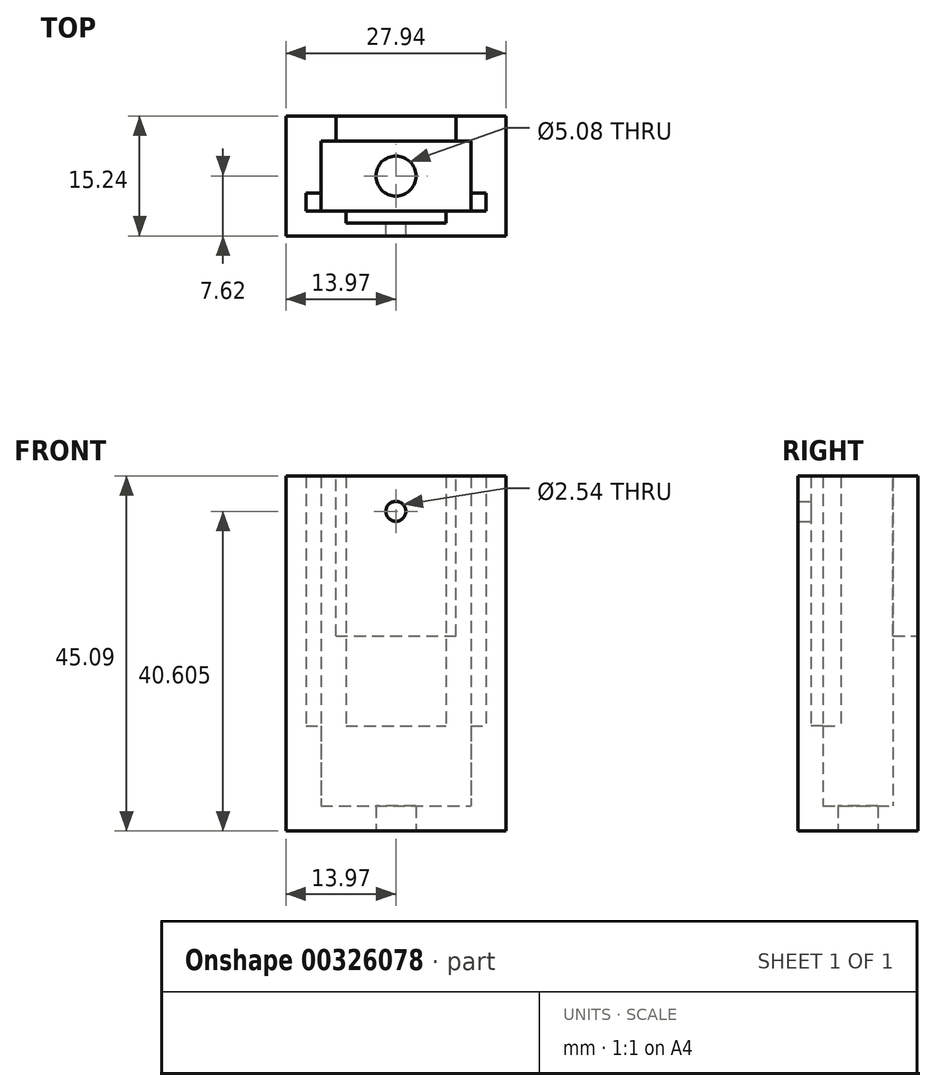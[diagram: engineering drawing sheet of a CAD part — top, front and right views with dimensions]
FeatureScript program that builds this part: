
annotation { "Feature Type Name" : "Feature", "Feature Type Description" : "" }
export const myFeature = defineFeature(function(context is Context, id is Id, definition is map)
    precondition{}
    {
        {
            var Q0;
            Q0=qCreatedBy(makeId("Top.planeOp"),FACE);
            var sketch = newSketch(context, id + "F0", { "sketchPlane" : qUnion([Q0])});
            skLineSegment(sketch, "E0.bottom", {"start": v(-13.97, -7.62) * mm, "end": v(13.97, -7.62) * mm});
            skLineSegment(sketch, "E0.top", {"start": v(-13.97, 7.62) * mm, "end": v(13.97, 7.62) * mm});
            skLineSegment(sketch, "E0.left", {"start": v(-13.97, -7.62) * mm, "end": v(-13.97, 7.62) * mm});
            skLineSegment(sketch, "E0.right", {"start": v(13.97, -7.62) * mm, "end": v(13.97, 7.62) * mm});
            skPoint(sketch, "E0.middle", {"position": v(0, 0) * mm});
            skCircle(sketch, "E1", {"center": v(0, 0) * mm, "radius": 2.54 * mm});
            skSolve(sketch);
        }
        {
            var Q0;
            Q0=makeQuery(id+"F0.imprint","IMPRINT",FACE,{"disambiguationData":[TD([[makeQuery(id+"F0.imprint","IMPRINT",EDGE,{"derivedFrom":sQuery(id+"F0.wireOp",EDGE,"E0.bottom")}),1.0]])]});
            extrude(context, id + "F1", {"entities" : qUnion([Q0]), "depth" : 3.17 * mm});
        }
        {
            var Q0;
            Q0=makeQuery(id+"F1.opExtrude","CAP_FACE",FACE,{"disambiguationData":[OSD([sQuery(id+"F0.wireOp",EDGE,"E0.bottom"),sQuery(id+"F0.wireOp",EDGE,"E0.top"),sQuery(id+"F0.wireOp",EDGE,"E0.left"),sQuery(id+"F0.wireOp",EDGE,"E0.right"),sQuery(id+"F0.wireOp",EDGE,"E1")])],"isStart":false});
            var sketch = newSketch(context, id + "F2", { "sketchPlane" : qUnion([Q0])});
            skLineSegment(sketch, "E2.bottom", {"start": v(-9.53, -4.45) * mm, "end": v(9.53, -4.45) * mm});
            skLineSegment(sketch, "E2.top", {"start": v(-9.53, 4.45) * mm, "end": v(9.53, 4.45) * mm});
            skLineSegment(sketch, "E2.left", {"start": v(-9.53, -4.45) * mm, "end": v(-9.53, 4.45) * mm});
            skLineSegment(sketch, "E2.right", {"start": v(9.53, -4.45) * mm, "end": v(9.53, 4.45) * mm});
            skPoint(sketch, "E2.middle", {"position": v(0, 0) * mm});
            skSolve(sketch);
        }
        {
            var Q0;
            Q0=makeQuery(id+"F2.imprint","IMPRINT",FACE,{"disambiguationData":[TD([[makeQuery(id+"F2.imprint","IMPRINT",EDGE,{"derivedFrom":sQuery(id+"F2.wireOp",EDGE,"E2.bottom")}),-1.0]])]});
            extrude(context, id + "F3", {"entities" : qUnion([Q0]), "operationType" : NewBodyOperationType.ADD, "depth" : 10.16 * mm});
        }
        {
            var Q0;
            Q0=makeQuery(id+"F3.opExtrude","CAP_FACE",FACE,{"disambiguationData":[OSD([sQuery(id+"F0.wireOp",EDGE,"E0.bottom"),sQuery(id+"F0.wireOp",EDGE,"E0.top"),sQuery(id+"F0.wireOp",EDGE,"E0.left"),sQuery(id+"F0.wireOp",EDGE,"E0.right"),sQuery(id+"F2.wireOp",EDGE,"E2.bottom"),sQuery(id+"F2.wireOp",EDGE,"E2.top"),sQuery(id+"F2.wireOp",EDGE,"E2.left"),sQuery(id+"F2.wireOp",EDGE,"E2.right")])],"isStart":false});
            var sketch = newSketch(context, id + "F4", { "sketchPlane" : qUnion([Q0])});
            skPoint(sketch, "E3", {"position": v(-11.43, -4.45) * mm});
            skLineSegment(sketch, "E4.bottom", {"start": v(-11.43, -4.45) * mm, "end": v(11.43, -4.45) * mm});
            skLineSegment(sketch, "E4.top", {"start": v(-11.43, -2.16) * mm, "end": v(11.43, -2.16) * mm});
            skLineSegment(sketch, "E4.left", {"start": v(-11.43, -4.45) * mm, "end": v(-11.43, -2.16) * mm});
            skLineSegment(sketch, "E4.right", {"start": v(11.43, -4.45) * mm, "end": v(11.43, -2.16) * mm});
            skLineSegment(sketch, "E5", {"start": v(0, -4.45) * mm, "end": v(-6.35, -4.45) * mm});
            skLineSegment(sketch, "E6.bottom", {"start": v(-6.35, -4.45) * mm, "end": v(6.35, -4.45) * mm});
            skLineSegment(sketch, "E6.top", {"start": v(-6.35, -5.97) * mm, "end": v(6.35, -5.97) * mm});
            skLineSegment(sketch, "E6.left", {"start": v(-6.35, -4.45) * mm, "end": v(-6.35, -5.97) * mm});
            skLineSegment(sketch, "E6.right", {"start": v(6.35, -4.45) * mm, "end": v(6.35, -5.97) * mm});
            skSolve(sketch);
        }
        {
            var Q0;
            {var subQ1=sQuery(id+"F4.wireOp",EDGE,"E4.left");Q0=makeQuery(id+"F4.imprint","IMPRINT",FACE,{"disambiguationData":[TD([[makeQuery(id+"F4.imprint","IMPRINT",EDGE,{"derivedFrom":subQ1}),1.0]])]});}
            extrude(context, id + "F5", {"entities" : qUnion([Q0]), "operationType" : NewBodyOperationType.ADD, "depth" : 31.75 * mm});
        }
        {
            var Q0;
            Q0=makeQuery(id+"F5.opExtrude","CAP_FACE",FACE,{"disambiguationData":[OSD([sQuery(id+"F0.wireOp",EDGE,"E0.bottom"),sQuery(id+"F0.wireOp",EDGE,"E0.top"),sQuery(id+"F0.wireOp",EDGE,"E0.left"),sQuery(id+"F0.wireOp",EDGE,"E0.right"),sQuery(id+"F2.wireOp",EDGE,"E2.top"),sQuery(id+"F2.wireOp",EDGE,"E2.left"),sQuery(id+"F2.wireOp",EDGE,"E2.right"),sQuery(id+"F4.wireOp",EDGE,"E4.bottom"),sQuery(id+"F4.wireOp",EDGE,"E4.top"),sQuery(id+"F4.wireOp",EDGE,"E4.left"),sQuery(id+"F4.wireOp",EDGE,"E4.right"),sQuery(id+"F4.wireOp",EDGE,"E6.top"),sQuery(id+"F4.wireOp",EDGE,"E6.left"),sQuery(id+"F4.wireOp",EDGE,"E6.right")])],"isStart":false});
            var sketch = newSketch(context, id + "F6", { "sketchPlane" : qUnion([Q0])});
            skPoint(sketch, "E7", {"position": v(-7.62, 4.45) * mm});
            skLineSegment(sketch, "E8.bottom", {"start": v(-7.62, 4.45) * mm, "end": v(7.62, 4.45) * mm});
            skLineSegment(sketch, "E8.top", {"start": v(-7.62, 7.62) * mm, "end": v(7.62, 7.62) * mm});
            skLineSegment(sketch, "E8.left", {"start": v(-7.62, 4.45) * mm, "end": v(-7.62, 7.62) * mm});
            skLineSegment(sketch, "E8.right", {"start": v(7.62, 4.45) * mm, "end": v(7.62, 7.62) * mm});
            skSolve(sketch);
        }
        {
            var Q0;
            Q0 = qSketchRegion(id + "F6", true);
            extrude(context, id + "F7", {"entities" : qUnion([Q0]), "operationType" : NewBodyOperationType.REMOVE, "oppositeDirection" : true, "depth" : 20.32 * mm});
        }
        {
            var Q0;
            Q0=makeQuery(id+"F5.opExtrude","SWEPT_FACE",FACE,{"disambiguationData":[OSD([sQuery(id+"F4.wireOp",EDGE,"E6.top")])]});
            var sketch = newSketch(context, id + "F8", { "sketchPlane" : qUnion([Q0])});
            skCircle(sketch, "E9", {"center": v(0, 40.6) * mm, "radius": 1.27 * mm});
            skSolve(sketch);
        }
        {
            var Q0;
            Q0 = qSketchRegion(id + "F8", true);
            extrude(context, id + "F9", {"entities" : qUnion([Q0]), "operationType" : NewBodyOperationType.REMOVE, "endBound" : BoundingType.UP_TO_NEXT, "oppositeDirection" : true, "depth" : 25.4 * mm});
        }
    });
